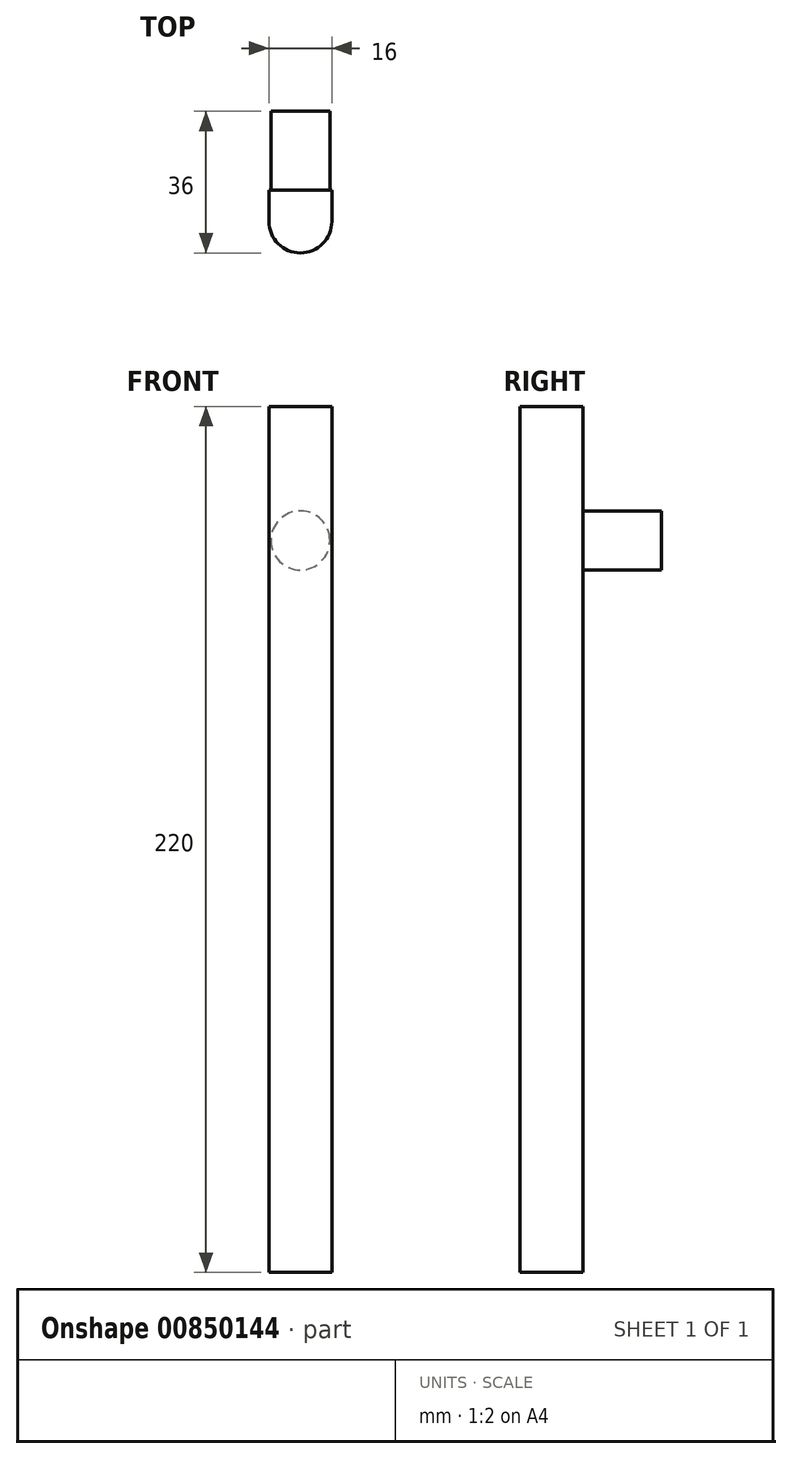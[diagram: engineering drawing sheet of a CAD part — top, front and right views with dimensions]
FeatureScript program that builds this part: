
annotation { "Feature Type Name" : "Feature", "Feature Type Description" : "" }
export const myFeature = defineFeature(function(context is Context, id is Id, definition is map)
    precondition{}
    {
        {
            var Q0;
            Q0=qCreatedBy(makeId("Top.planeOp"),FACE);
            var sketch = newSketch(context, id + "F0", { "sketchPlane" : qUnion([Q0])});
            skLineSegment(sketch, "E0.bottom", {"start": v(-8.28, 3.93) * mm, "end": v(7.72, 3.93) * mm});
            skLineSegment(sketch, "E0.top", {"start": v(-8.28, -12.07) * mm, "end": v(7.72, -12.07) * mm});
            skLineSegment(sketch, "E0.left", {"start": v(-8.28, 3.93) * mm, "end": v(-8.28, -12.07) * mm});
            skLineSegment(sketch, "E0.right", {"start": v(7.72, 3.93) * mm, "end": v(7.72, -12.07) * mm});
            skSolve(sketch);
        }
        {
            var Q0;
            Q0=makeQuery(id+"F0.imprint","IMPRINT",FACE,{"disambiguationData":[TD([[makeQuery(id+"F0.imprint","IMPRINT",EDGE,{"derivedFrom":sQuery(id+"F0.wireOp",EDGE,"E0.bottom")}),-1.0]])]});
            extrude(context, id + "F1", {"entities" : qUnion([Q0]), "depth" : 220 * mm, "offsetDistance" : 25 * mm});
        }
        {
            var Q0;
            Q0=makeQuery(id+"F1.opExtrude","SWEPT_EDGE",EDGE,{"disambiguationData":[OSD([sQuery(id+"F0.wireOp",EDGE,"E0.top"),sQuery(id+"F0.wireOp",EDGE,"E0.left")])]});
            var Q1;
            Q1=makeQuery(id+"F1.opExtrude","SWEPT_EDGE",EDGE,{"disambiguationData":[OSD([sQuery(id+"F0.wireOp",EDGE,"E0.top"),sQuery(id+"F0.wireOp",EDGE,"E0.right")])]});
            fillet(context, id + "F2", {"entities" : qUnion([Q0, Q1]), "radius" : 8 * mm, "tangentPropagation" : true, "allowEdgeOverflow" : false});
        }
        {
            var Q0;
            Q0=makeQuery(id+"F1.opExtrude","SWEPT_FACE",FACE,{"disambiguationData":[OSD([sQuery(id+"F0.wireOp",EDGE,"E0.bottom")])]});
            var sketch = newSketch(context, id + "F3", { "sketchPlane" : qUnion([Q0])});
            skCircle(sketch, "E1", {"center": v(0.28, 185.95) * mm, "radius": 7.5 * mm});
            skSolve(sketch);
        }
        {
            var Q0;
            Q0=makeQuery(id+"F3.imprint","IMPRINT",FACE,{"disambiguationData":[TD([[makeQuery(id+"F3.imprint","IMPRINT",EDGE,{"derivedFrom":sQuery(id+"F3.wireOp",EDGE,"E1")}),1.0]])]});
            extrude(context, id + "F4", {"entities" : qUnion([Q0]), "operationType" : NewBodyOperationType.ADD, "depth" : 20 * mm, "offsetDistance" : 25 * mm});
        }
    });
